SOLIDWORKS PART (.sldprt)
format: sldprt  version: not decoded by parser v0  size: 709,632 bytes
history: native  units: mm
features: sketch x27, revolve x18, cut_extrude x8, plane x6, material x1, extrude x1, pattern_circular x1 (+16 scaffold rows collapsed)
feature tree (78):
  scaffold x16  (default folders/planes/origin — collapsed)
  material  "Material <not specified>"
  sketch  "Sketch1"  dims[D1=20500.0mm D2=1110.0mm D3=1300.0mm D4=550.0mm D5=200.0mm D6=10.0mm]
  revolve  "Revolve1"  Angle=360deg
  plane  "50"
  plane  "65-245"
  plane  "140"
  plane  "202"
  plane  "290"
  plane  "300"
  sketch  "Sketch2"  dims[D1=18750.0mm D2=5.16mm D3=73.15mm D4=200.0mm D5=180.0mm D6=~1234.34193mm]
  revolve  "N3"  Angle=360deg
  sketch  "Sketch3"  dims[D1=4450.0mm D2=33.53mm D3=3.38mm D4=160.0mm D5=150.0mm]
  revolve  "N4"  Angle=360deg
  sketch  "Sketch4"  dims[D1=3.38mm D2=33.53mm D3=160.0mm D4=150.0mm D5=19600.0mm]
  revolve  "N2"  Angle=360deg
  sketch  "Sketch5"  dims[D1=5.49mm D2=88.9mm D3=200.0mm D4=180.0mm]
  revolve  "N5"  Angle=360deg
  sketch  "Sketch6"  dims[D1=5.49mm D2=88.9mm D3=200.0mm D4=180.0mm D5=500.0mm]
  revolve  "N6"  Angle=360deg
  sketch  "Sketch7"  dims[D1=5.49mm D2=88.9mm D3=240.0mm D4=220.0mm]
  revolve  "N7"  Angle=360deg
  sketch  "Sketch8"  dims[D1=3100.0mm D2=6.4mm D3=610.0mm D4=220.0mm D5=150.0mm]
  revolve  "N8"  Angle=360deg
  sketch  "Sketch9"
  cut_extrude  "Extrude1"  Depth=220mm
  sketch  "Sketch10"  dims[D1=5.49mm D2=2400.0mm D3=88.9mm D4=200.0mm D5=200.0mm]
  revolve  "N9"  Angle=360deg
  sketch  "Sketch11"  dims[D1=5.49mm D2=88.9mm D3=180.0mm D4=200.0mm D5=600.0mm]
  revolve  "N10"  Angle=360deg
  sketch  "Sketch12"  dims[D1=5.49mm D2=200.0mm D3=88.9mm D4=2400.0mm D5=180.0mm]
  revolve  "N11"  Angle=360deg
  sketch  "Sketch13"  dims[D1=5.49mm D2=200.0mm D3=88.9mm D4=180.0mm D5=600.0mm]
  revolve  "N12"  Angle=360deg
  sketch  "Sketch14"  dims[D1=5.0mm D2=324.0mm D3=160.0mm D4=150.0mm D5=3800.0mm]
  revolve  "N13"  Angle=360deg
  sketch  "Sketch15"
  cut_extrude  "Extrude2"  Depth=180mm
  sketch  "Sketch16"  dims[D1=8.89mm D2=609.6mm D3=260.0mm D4=220.0mm D5=1000.0mm]
  revolve  "Revolve16"  Angle=360deg
  sketch  "Sketch17"
  cut_extrude  "Extrude3"  Depth=280mm
  sketch  "Sketch18"  dims[D1=19050.0mm D2=8.99mm D3=260.0mm D4=609.6mm D5=200.0mm]
  revolve  "Revolve17"  Angle=360deg
  sketch  "Sketch19"
  cut_extrude  "Extrude4"  Depth=260mm
  sketch  "Sketch20"  dims[D1=11550.0mm D2=200.0mm D3=260.0mm D4=8.89mm D5=609.6mm]
  revolve  "Revolve18"  Angle=360deg
  sketch  "Sketch21"
  cut_extrude  "Extrude5"  Depth=260mm
  sketch  "Sketch22"  dims[D1=457.2mm D2=8.89mm D3=240.0mm D4=200.0mm D5=12800.0mm]
  revolve  "Revolve19"  Angle=360deg
  sketch  "Sketch23"
  cut_extrude  "Extrude6"  Depth=240mm
  sketch  "Sketch24"  dims[D1=240.0mm D2=8.89mm D3=457.2mm D4=200.0mm D5=5200.0mm]
  revolve  "Revolve20"  Angle=360deg
  sketch  "Sketch25"
  cut_extrude  "Extrude7"  Depth=240mm
  sketch  "Sketch26"  dims[D1=0.0mm D2=165.0mm]
  extrude  "Extrude8"  Depth=320mm
  sketch  "Sketch27"  dims[D1=50.0mm D2=1200.0mm]
  cut_extrude  "Extrude9"  [1 undecoded]
  pattern_circular  "CirPattern1"  Count=16 Angle=360deg
decode coverage: 47 of 55 modeling features carry decoded parameters
note: ~ marks probable driven/reference dimensions
note: 1 parameter value undecoded
note: suppression state not decoded; provenance and decode notes live in map.json
